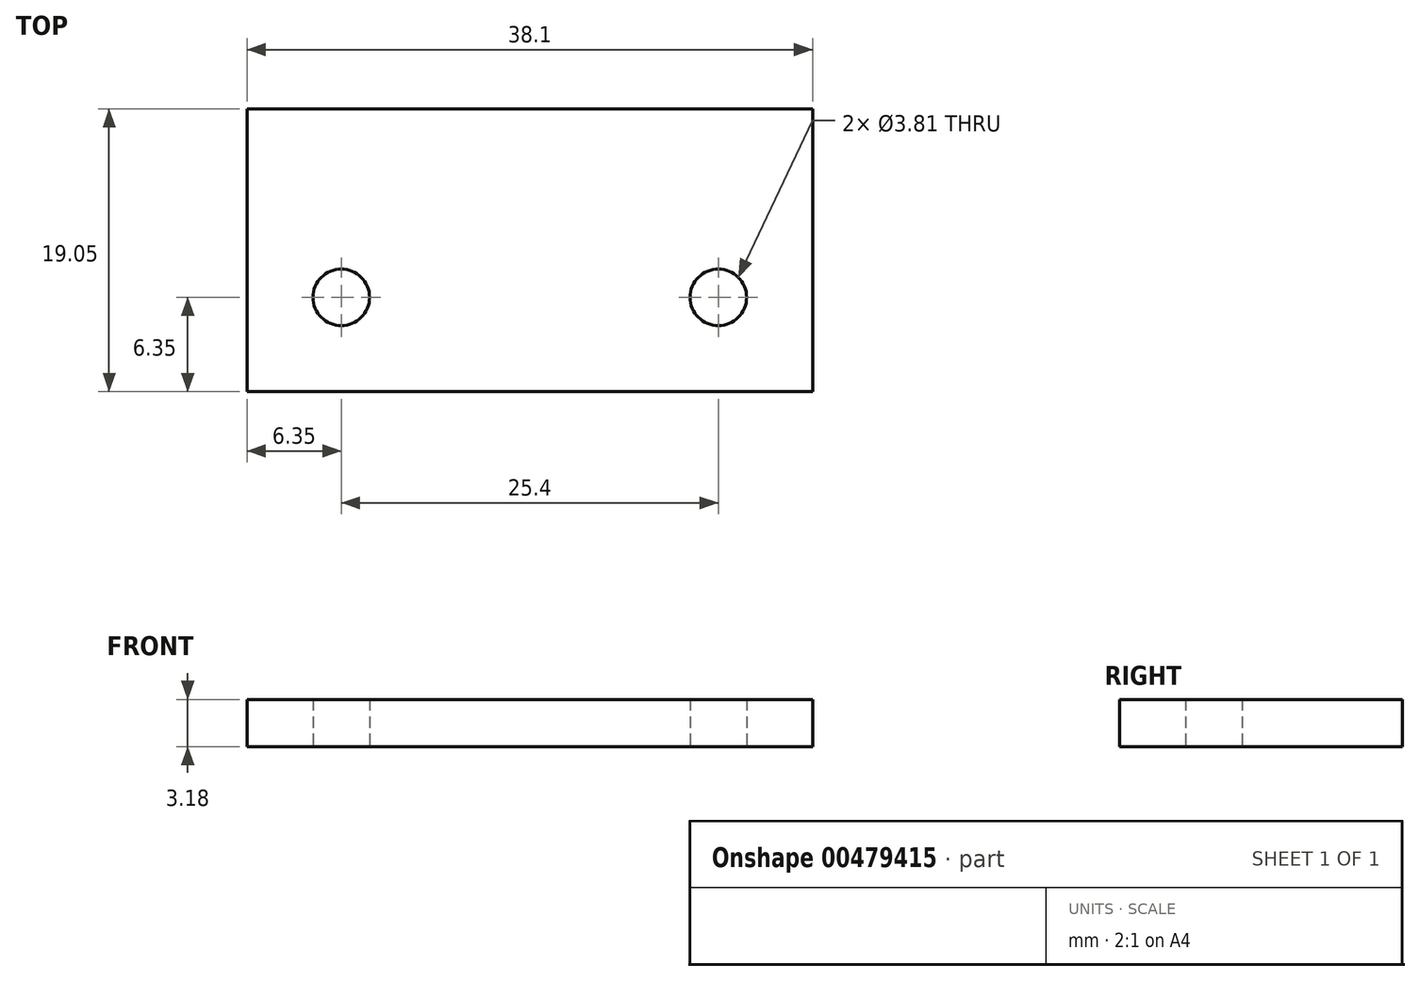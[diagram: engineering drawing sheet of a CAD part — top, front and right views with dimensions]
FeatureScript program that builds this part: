
annotation { "Feature Type Name" : "Feature", "Feature Type Description" : "" }
export const myFeature = defineFeature(function(context is Context, id is Id, definition is map)
    precondition{}
    {
        {
            var Q0;
            Q0=qCreatedBy(makeId("Top.planeOp"),FACE);
            var sketch = newSketch(context, id + "F0", { "sketchPlane" : qUnion([Q0])});
            skLineSegment(sketch, "E0.bottom", {"start": v(0, 0) * mm, "end": v(38.1, 0) * mm});
            skLineSegment(sketch, "E0.top", {"start": v(0, 19.05) * mm, "end": v(38.1, 19.05) * mm});
            skLineSegment(sketch, "E0.left", {"start": v(0, 0) * mm, "end": v(0, 19.05) * mm});
            skLineSegment(sketch, "E0.right", {"start": v(38.1, 0) * mm, "end": v(38.1, 19.05) * mm});
            skCircle(sketch, "E1", {"center": v(6.35, 6.35) * mm, "radius": 1.9 * mm});
            skCircle(sketch, "E2", {"center": v(31.75, 6.35) * mm, "radius": 1.9 * mm});
            skSolve(sketch);
        }
        {
            var Q0;
            Q0 = qSketchRegion(id + "F0", true);
            extrude(context, id + "F1", {"entities" : qUnion([Q0]), "depth" : 3.17 * mm, "offsetDistance" : 25.4 * mm});
        }
    });
